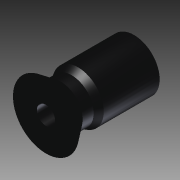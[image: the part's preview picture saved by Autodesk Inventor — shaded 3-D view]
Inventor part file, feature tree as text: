
AUTODESK INVENTOR PART (.ipt)
format: ipt  version: 2011 SP1 (Build 150282100, 282)  size: 94,208 bytes
history: native  units: mm
features: other x14, revolve x1, sketch x1
ambient origin geometry x8: Origin, YZ Plane, XZ Plane, XY Plane, X Axis, Y Axis, Z Axis, Center Point
bodies: Solid1 (feature_tree)
feature tree (16):
  revolve  "Revolution1"  [1 undecoded]
  other  "PAD_DUMMY_XY"
  other  "PAD_DUMMY_YZ"
  other  "PAD_DUMMY_ZX"
  other  "PAD_DUMMY_X"
  other  "PAD_DUMMY_Y"
  other  "PAD_DUMMY_Z"
  other  "PAD_DUMMY_Center"
  other  "pad_a_XY"
  other  "pad_a_YZ"
  other  "pad_a_ZX"
  other  "pad_a_X"
  other  "pad_a_Y"
  other  "pad_a_Z"
  other  "pad_a_Center"
  sketch  "Sketch_3"  dims[d0=360.0deg d1=0.0mm d2=0.0mm]
note: 1 required parameter value undecoded (feature->parameter linkage not recoverable at this tier; creation-order binding heuristic only, values carry confidence <= 0.55)
